# Revit family: BIMLIB_H-образный_клапан_РОСТерм
name_source: partatom
category: Арматура трубопроводов
revit_build: Autodesk Revit 2017 (Build: 20170118_1100(x64)
units: mm (PartAtom-declared; Revit-internal decimal feet)

## family parameters
Всегда вертикально = Нет
На основе рабочей плоскости = Нет
Общий = Нет
При загрузке вырезать с полостями = Нет
Размер круглого соединителя = Использовать диаметр
Тип детали = Клапан - Вставляется

## types (1)
- HEIZEN HDD
    ADSK_URL документации изделия = http://rostherm.ru
    ADSK_URL страницы изделия = http://rostherm.ru
    ADSK_Версия Revit = 2017
    ADSK_Единица измерения = шт.
    ADSK_Завод-изготовитель = Heizen
    ADSK_Код изделия = HDD 345-15
    ADSK_Марка = HDD 345-15
    ADSK_Масса = 0
    ADSK_Материал = BIMLIB_Латунь_РТ
    ADSK_Наименование = Н-ОБРАЗНЫЙ КЛАПАН HDD 345-15
    ADSK_Наименование краткое = HDD 345-15
    ADSK_Обозначение = ГОСТ 5761-2005
    BL_BIM library = https://bimlib.pro
    URL = http://rostherm.ru
    Изготовитель = РОСТерм
    Коэффициент K = 0
    Метод определения потерь = Не задано
    Описание = Клапан Н-образный HDD
    РТ_DN_1 = 15 мм
    РТ_DN_2 = 20 мм
    РТ_L = 51 мм
    РТ_L1 = 25.5 мм
    РТ_L2 = 25.5 мм
    РТ_Номинальное давление = 10.0 бары
